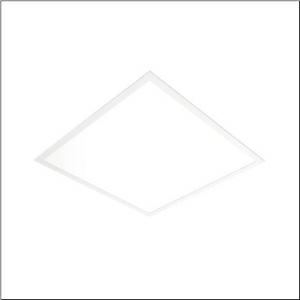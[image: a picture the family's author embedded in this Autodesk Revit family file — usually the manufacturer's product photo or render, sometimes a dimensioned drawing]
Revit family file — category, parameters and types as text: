
# Revit family: apollon_41_51mh11wm2443
name_source: partatom
category: Lighting Fixtures
units: mm (PartAtom-declared; Revit-internal decimal feet)

## family parameters
Cut with Voids When Loaded = No
Host = Face
Light Source = No
Part Type = Normal
Room Calculation Point = No
Round Connector Dimension = Use Diameter
Shared = No

## types (1)
- --- (1 x LED, 4380 lm, 35 W, 4000K)
    Apparent Load = 35 VA
    CIE Flux Codes = 61 87 97 100 100
    Color Rendering = 80
    Color Temperature = 4000K
    Default Elevation = 1800 mm
    Description = Apollon 41, office luminaire, primary optical cover: prismatic diffuser, of PS, light emission: direct distribution, primary light characteristic: symmetric, installation type: lay-in mounting, LED, rated luminous flux: 4.375lm, luminous efficacy: 125lm/W, light colour: 840, colour temperature: 4000K, control gear: ON/OFF Multilumen, with terminal, 3-pole, mains connection: 220..240V, AC, 50/60Hz, rated input power: 35W, suitable for self-contained emergency lighting element 58DB00B013A with integrated self-test function according to EN 60598-2-22, housing, of aluminium section, traffic white (RAL 9016), module: M625, length: 620mm, width: 620mm, height: 60mm, recess depth: 180mm, housing upper side, of sheet steel, protection rating (complete): IP20, protection rating (lamp compartment, on room side): IP40, insulation class (complete): insulation class II (safety insulation), certification: CE, ENEC, impact resistance: IK03, permissible operating ambient temperature: -25..+40°C, packaging unit: 1 piece
    Height = 0 mm  [stored 0 ft]
    Lamp = 1 x LED
    Lamp Light Flux = 4380 lm
    Lamp Power = 35 W
    Lamp count = 1
    Length = 620 mm
    Luminous efficacy = 125 lm/W
    Manufacturer = Siteco
    ModVariant = No
    Model = 51MH11WM2443
    Mounting Place = Ceiling
    Mounting Type = Recessed
    Number of Poles = 1
    OnlyDefault = Yes
    Power Factor = 1
    Product Name = Apollon 41
    Product group = office luminaire | ceiling recessed
    ProductGroupID = 400
    Protection Class = Protection class II
    Protection Degree = IP 20
    RLX_Detail_Level = 1
    RLX_Emergency_Light_Flux = 0 lm
    RLX_Emergency_Type = 0
    RLX_Emergency_Type_DB = No
    RlxData = <blob elided: 13121 chars, md5=f5de4f74>
    Socket = socket
    Standby Power = 0 W
    System Light Flux = 4380 lm
    System Power = 35 W
    Type Comments = factory setting: luminous flux: 100 % | (ON | ON) | 900 mA
    Type Image = l_1291024.jpg
    URL = http://relux.com
    VarID = @adj_033421
    Voltage = 0 V
    Weight = 0.00 kg
    Width = 620 mm

note: [stored X ft] marks values corroborated as IEEE doubles in the binary element streams (Revit-internal decimal feet)

## geometry (parser evidence)
native form markers: Sweep x11
no freeform markers — native parametric forms only
